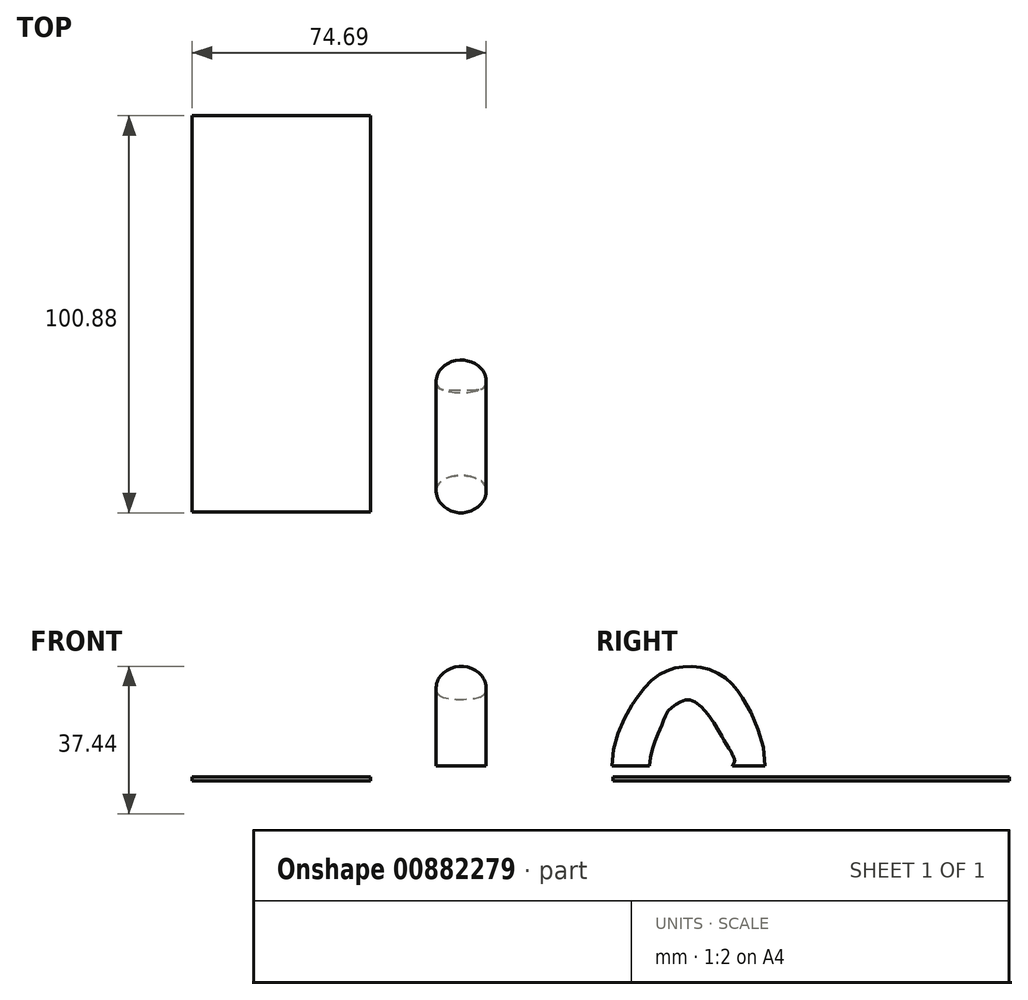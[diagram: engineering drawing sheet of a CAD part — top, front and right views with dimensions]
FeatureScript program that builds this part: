
annotation { "Feature Type Name" : "Feature", "Feature Type Description" : "" }
export const myFeature = defineFeature(function(context is Context, id is Id, definition is map)
    precondition{}
    {
        {
            var Q0;
            Q0=qCreatedBy(makeId("Top.planeOp"),FACE);
            var sketch = newSketch(context, id + "F0", { "sketchPlane" : qUnion([Q0])});
            skLineSegment(sketch, "E0.bottom", {"start": v(-68.34, 54.43) * mm, "end": v(-23, 54.43) * mm});
            skLineSegment(sketch, "E0.top", {"start": v(-68.34, -46.2) * mm, "end": v(-23, -46.2) * mm});
            skLineSegment(sketch, "E0.left", {"start": v(-68.34, 54.43) * mm, "end": v(-68.34, -46.2) * mm});
            skLineSegment(sketch, "E0.right", {"start": v(-23, 54.43) * mm, "end": v(-23, -46.2) * mm});
            skSolve(sketch);
        }
        {
            var Q0;
            Q0=makeQuery(id+"F0.imprint","IMPRINT",FACE,{"disambiguationData":[TD([[makeQuery(id+"F0.imprint","IMPRINT",EDGE,{"derivedFrom":sQuery(id+"F0.wireOp",EDGE,"E0.bottom")}),-1.0]])]});
            extrude(context, id + "F1", {"entities" : qUnion([Q0]), "depth" : 1.02 * mm, "offsetDistance" : 25.4 * mm});
        }
        {
            var Q0;
            Q0=qCreatedBy(makeId("Top.planeOp"),FACE);
            var sketch = newSketch(context, id + "F2", { "sketchPlane" : qUnion([Q0])});
            skCircle(sketch, "E1", {"center": v(0, 46.91) * mm, "radius": 6.35 * mm});
            skCircle(sketch, "E2", {"center": v(0, -39.25) * mm, "radius": 6.35 * mm});
            skSolve(sketch);
        }
        {
            var Q0;
            Q0=qCreatedBy(makeId("Right.planeOp"),FACE);
            var sketch = newSketch(context, id + "F3", { "sketchPlane" : qUnion([Q0])});
            skFitSpline(sketch, "E3", {"points": [v(-39.12, 0) * mm, v(-36.62, 17.29) * mm, v(-30.2, 23) * mm, v(-24.49, 23.36) * mm, v(-17.89, 18.36) * mm, v(-14.67, 0) * mm, v(-39.12, 0) * mm]});
            skSolve(sketch);
        }
        {
            var Q0;
            Q0=makeQuery(id+"F2.imprint","IMPRINT",FACE,{"disambiguationData":[TD([[makeQuery(id+"F2.imprint","IMPRINT",EDGE,{"derivedFrom":sQuery(id+"F2.wireOp",EDGE,"E2")}),1.0]])]});
            var Q1;
            Q1=sQuery(id+"F3.wireOp",EDGE,"E3");
            sweep(context, id + "F4", {"profiles" : qUnion([Q0]), "path" : qUnion([Q1])});
        }
        {
            var Q0;
            Q0=qCreatedBy(makeId("Top.planeOp"),FACE);
            cPlane(context, id + "F5", {"entities" : qUnion([Q0]), "cplaneType" : CPlaneType.OFFSET, "offset" : 3.8 * mm, "width" : 152.4 * mm, "height" : 152.4 * mm});
        }
        {
            var Q0;
            Q0=qCreatedBy(id+"F5.planeOp",FACE);
            var sketch = newSketch(context, id + "F6", { "sketchPlane" : qUnion([Q0])});
            skLineSegment(sketch, "E4", {"start": v(-10.22, -3.22) * mm, "end": v(-10.22, -50.01) * mm});
            skLineSegment(sketch, "E5", {"start": v(-10.22, -50.01) * mm, "end": v(10.34, -50.01) * mm});
            skLineSegment(sketch, "E6", {"start": v(10.34, -50.01) * mm, "end": v(10.34, -1.13) * mm});
            skLineSegment(sketch, "E7", {"start": v(10.34, -1.13) * mm, "end": v(-10.22, -3.22) * mm});
            skSolve(sketch);
        }
        {
            var Q0;
            Q0=makeQuery(id+"F6.imprint","IMPRINT",FACE,{"disambiguationData":[TD([[makeQuery(id+"F6.imprint","IMPRINT",EDGE,{"derivedFrom":sQuery(id+"F6.wireOp",EDGE,"E4")}),1.0]])]});
            extrude(context, id + "F7", {"entities" : qUnion([Q0]), "operationType" : NewBodyOperationType.REMOVE, "oppositeDirection" : true, "depth" : 25.4 * mm, "offsetDistance" : 25.4 * mm});
        }
    });
